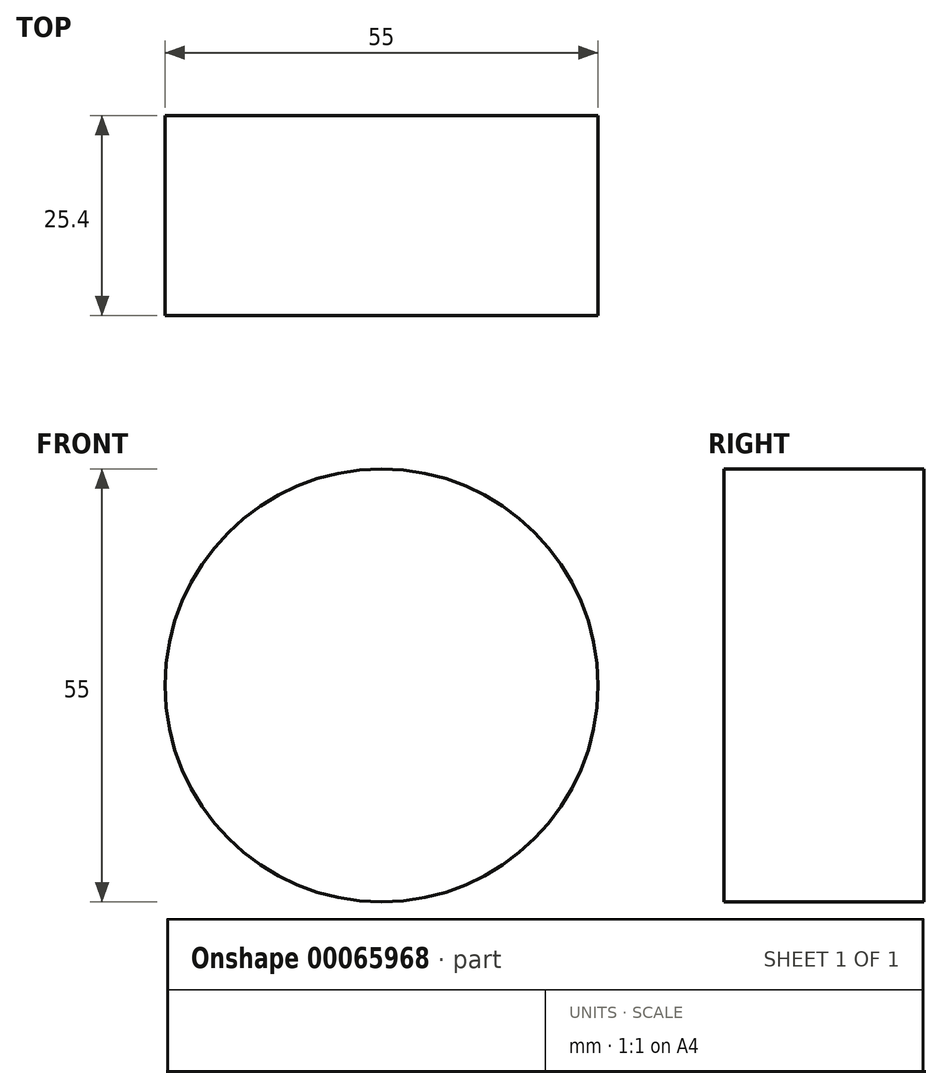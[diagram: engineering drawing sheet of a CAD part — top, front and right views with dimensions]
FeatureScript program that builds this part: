
annotation { "Feature Type Name" : "Feature", "Feature Type Description" : "" }
export const myFeature = defineFeature(function(context is Context, id is Id, definition is map)
    precondition{}
    {
        {
            var Q0;
            Q0=qCreatedBy(makeId("Front.planeOp"),FACE);
            var sketch = newSketch(context, id + "F0", { "sketchPlane" : qUnion([Q0])});
            skCircle(sketch, "E0", {"center": v(-4.68, 10.87) * mm, "radius": 27.5 * mm});
            skCircle(sketch, "E1", {"center": v(-4.68, 10.87) * mm, "radius": 20.5 * mm});
            skCircle(sketch, "E2", {"center": v(-18.57, 10.87) * mm, "radius": 3.38 * mm});
            skCircle(sketch, "E3", {"center": v(-4.99, 25.97) * mm, "radius": 3.16 * mm});
            skCircle(sketch, "E4", {"center": v(6.22, 21.27) * mm, "radius": 4 * mm});
            skText(sketch, "E5", { "text": "AC", "fontName": "OpenSans-Bold.ttf"});
            const initialGuessF0  = {"E5": [-0.01402, 0.00347, 1, 0, 0.01234]};
            skSetInitialGuess(sketch, initialGuessF0);
            skSolve(sketch);
        }
        {
            var Q0;
            Q0 = qSketchRegion(id + "F0", true);
            var Q1;
            Q1=makeQuery(id+"F0.imprint","IMPRINT",FACE,{"disambiguationData":[TD([[makeQuery(id+"F0.imprint","IMPRINT",EDGE,{"derivedFrom":sQuery(id+"F0.wireOp",EDGE,"E0")}),1.0]])]});
            var Q2;
            Q2=makeQuery(id+"F0.imprint","IMPRINT",FACE,{"disambiguationData":[TD([[makeQuery(id+"F0.imprint","IMPRINT",EDGE,{"derivedFrom":sQuery(id+"F0.wireOp",EDGE,"E4")}),1.0]])]});
            var Q3;
            Q3=makeQuery(id+"F0.imprint","IMPRINT",FACE,{"disambiguationData":[TD([[makeQuery(id+"F0.imprint","IMPRINT",EDGE,{"derivedFrom":sQuery(id+"F0.wireOp",EDGE,"E5.sketch_text.stroke-12")}),-1.0]])]});
            var Q4;
            Q4=makeQuery(id+"F0.imprint","IMPRINT",FACE,{"disambiguationData":[TD([[makeQuery(id+"F0.imprint","IMPRINT",EDGE,{"derivedFrom":sQuery(id+"F0.wireOp",EDGE,"E5.sketch_text.stroke-0")}),-1.0]])]});
            var Q5;
            Q5=makeQuery(id+"F0.imprint","IMPRINT",FACE,{"disambiguationData":[TD([[makeQuery(id+"F0.imprint","IMPRINT",EDGE,{"derivedFrom":sQuery(id+"F0.wireOp",EDGE,"E1")}),1.0]])]});
            var Q6;
            Q6=makeQuery(id+"F0.imprint","IMPRINT",FACE,{"disambiguationData":[TD([[makeQuery(id+"F0.imprint","IMPRINT",EDGE,{"derivedFrom":sQuery(id+"F0.wireOp",EDGE,"E2")}),1.0]])]});
            var Q7;
            Q7=makeQuery(id+"F0.imprint","IMPRINT",FACE,{"disambiguationData":[TD([[makeQuery(id+"F0.imprint","IMPRINT",EDGE,{"derivedFrom":sQuery(id+"F0.wireOp",EDGE,"E3")}),1.0]])]});
            var Q8;
            Q8=makeQuery(id+"F0.imprint","IMPRINT",FACE,{"disambiguationData":[TD([[makeQuery(id+"F0.imprint","IMPRINT",EDGE,{"derivedFrom":sQuery(id+"F0.wireOp",EDGE,"E5.sketch_text.stroke-8")}),1.0]])]});
            extrude(context, id + "F1", {"entities" : qUnion([Q0, Q1, Q2, Q3, Q4, Q5, Q6, Q7, Q8]), "depth" : 25.4 * mm});
        }
    });
